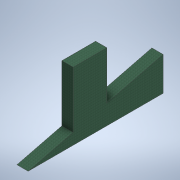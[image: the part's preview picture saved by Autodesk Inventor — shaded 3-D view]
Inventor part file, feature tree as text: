
AUTODESK INVENTOR PART (.ipt)
format: ipt  version: 2020.2 (Build 242310000, 310)  size: 114,176 bytes
history: native  units: in
note: dims shown in document units (in); Inventor stores cm internally (conversion verified against a paired STEP export)
features: extrude x2, sketch x2
ambient origin geometry x8: Origin, YZ Plane, XZ Plane, XY Plane, X Axis, Y Axis, Z Axis, Center Point
bodies: Solid1 (feature_tree)
feature tree (4):
  extrude  "Extrusion1"  Depth=12.0in
  extrude  "Extrusion2"  Depth=12.0in TaperAngle=0.0deg
  sketch  "Sketch1"  dims[d3=12.0in d4=0.0in d5=48.0in]
  sketch  "Sketch2"  dims[d6=36.0in d7=12.0in d8=0.0in]
